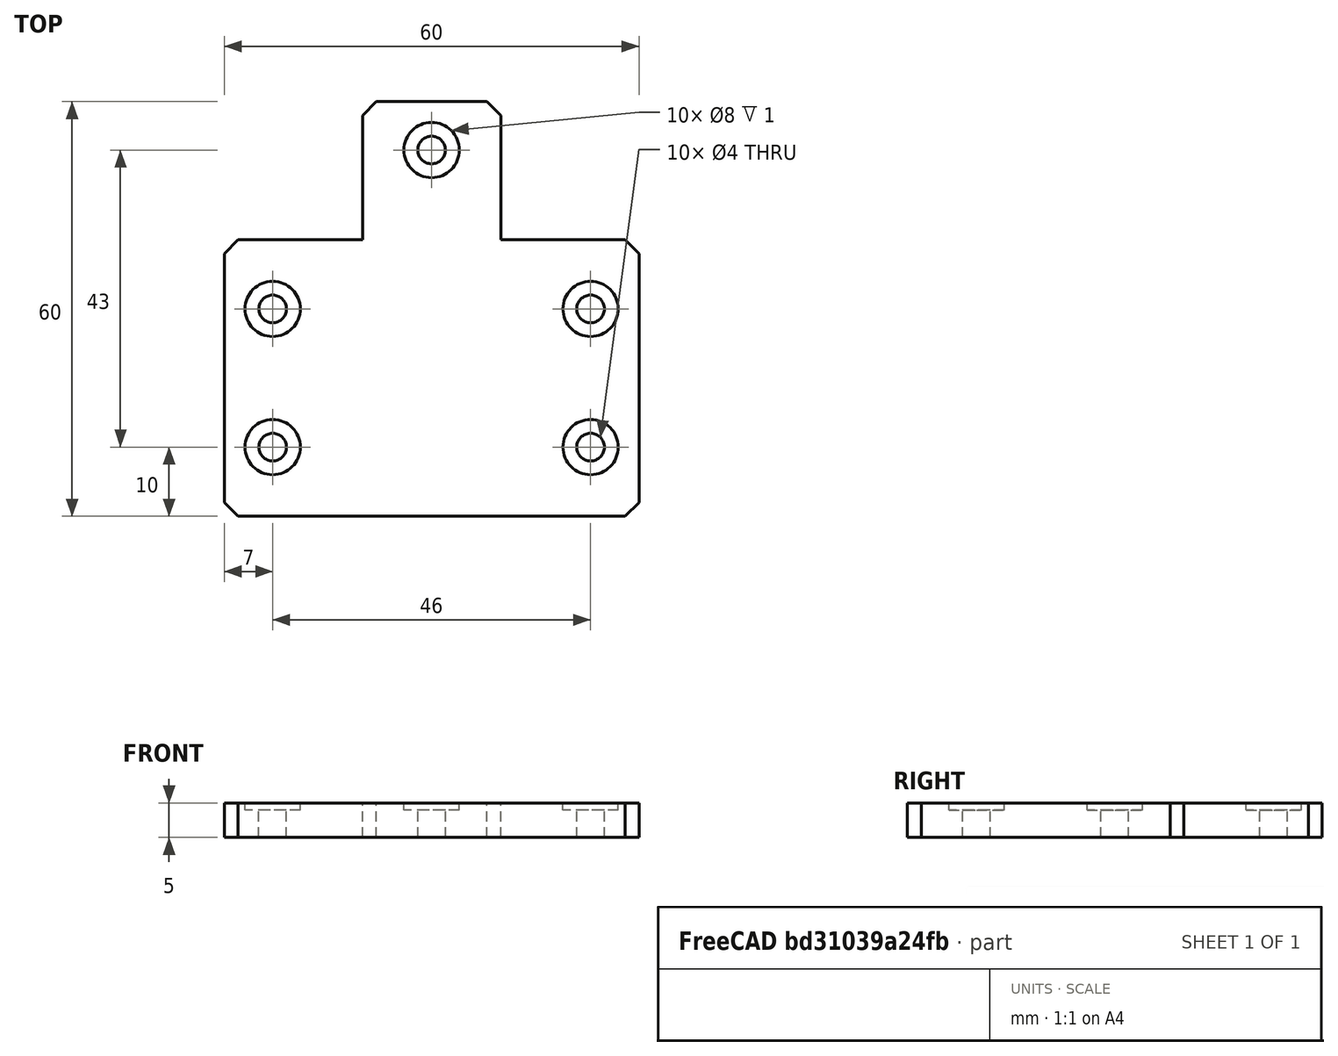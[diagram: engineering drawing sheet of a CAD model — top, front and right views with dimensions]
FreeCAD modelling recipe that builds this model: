
FCSTD DOCUMENT  (FreeCAD 0.18R14555 (Git shallow))
Label: t-bracket
License: All rights reserved
LicenseURL: http://en.wikipedia.org/wiki/All_rights_reserved
objects: Part::Cylinder×10, Part::MultiFuse×3, Part::Box×2, Part::Cut×2, Part::Feature×2, Part::Chamfer×1
note: 20 computed .brp shape members not serialized (recipe doc carries the construction recipe); baked Part::Feature solids carry a one-line shape summary decoded from their .brp

FEATURE [Part::Box] Box  label="Cube"
  AttacherType = Attacher::AttachEngine3D
  Height = 5
  Length = 60
  Width = 40
FEATURE [Part::Box] Box001  label="Cube001"
  AttacherType = Attacher::AttachEngine3D
  Height = 5
  Length = 20
  Placement = pos=(20,40,0) rot=(0,0,1;0rad)
  Width = 20
FEATURE [Part::MultiFuse] Fusion
  Shapes = -> [Box001,Box]
FEATURE [Part::Cylinder] Cylinder
  Angle = 360
  AttacherType = Attacher::AttachEngine3D
  Height = 10
  Placement = pos=(7,10,0) rot=(0,0,1;0rad)
  Radius = 2
FEATURE [Part::Cylinder] Cylinder001
  Angle = 360
  AttacherType = Attacher::AttachEngine3D
  Height = 10
  Placement = pos=(7,30,0) rot=(0,0,1;0rad)
  Radius = 2
FEATURE [Part::Cylinder] Cylinder002
  Angle = 360
  AttacherType = Attacher::AttachEngine3D
  Height = 10
  Placement = pos=(53,10,0) rot=(0,0,1;0rad)
  Radius = 2
FEATURE [Part::Cylinder] Cylinder003
  Angle = 360
  AttacherType = Attacher::AttachEngine3D
  Height = 10
  Placement = pos=(53,30,0) rot=(0,0,1;0rad)
  Radius = 2
FEATURE [Part::Cylinder] Cylinder004
  Angle = 360
  AttacherType = Attacher::AttachEngine3D
  Height = 10
  Placement = pos=(30,53,0) rot=(0,0,1;0rad)
  Radius = 2
FEATURE [Part::Cylinder] Cylinder005
  Angle = 360
  AttacherType = Attacher::AttachEngine3D
  Height = 1
  Placement = pos=(7,30,0) rot=(0,0,1;0rad)
  Radius = 4
FEATURE [Part::Cylinder] Cylinder006
  Angle = 360
  AttacherType = Attacher::AttachEngine3D
  Height = 1
  Placement = pos=(7,10,0) rot=(0,0,1;0rad)
  Radius = 4
FEATURE [Part::Cylinder] Cylinder007
  Angle = 360
  AttacherType = Attacher::AttachEngine3D
  Height = 1
  Placement = pos=(53,10,0) rot=(0,0,1;0rad)
  Radius = 4
FEATURE [Part::Cylinder] Cylinder008
  Angle = 360
  AttacherType = Attacher::AttachEngine3D
  Height = 1
  Placement = pos=(53,30,0) rot=(0,0,1;0rad)
  Radius = 4
FEATURE [Part::Cylinder] Cylinder009
  Angle = 360
  AttacherType = Attacher::AttachEngine3D
  Height = 1
  Placement = pos=(30,53,0) rot=(0,0,1;0rad)
  Radius = 4
FEATURE [Part::MultiFuse] Fusion001
  Placement = pos=(0,0,4) rot=(0,0,1;0rad)
  Shapes = -> [Cylinder006,Cylinder005,Cylinder009,Cylinder008,Cylinder007]
FEATURE [Part::MultiFuse] Fusion002
  Shapes = -> [Cylinder,Cylinder001,Cylinder003,Cylinder004,Cylinder002]
FEATURE [Part::Cut] Cut
  Base = -> Fusion
  Tool = -> Fusion001
FEATURE [Part::Cut] Cut001
  Base = -> Cut
  Tool = -> Fusion002
FEATURE [Part::Chamfer] Chamfer
  Base = -> Cut001
  Edges = 6 edges r=2: [Edge1,Edge3,Edge6,Edge25,Edge39,Edge52]
FEATURE [Part::Feature] Chamfer001
  shape: bbox 60 x 60 x 5 mm, 31 faces (baked)
FEATURE [Part::Feature] Chamfer001_solid  label="Chamfer001 (Solid)"
  shape: bbox 60 x 60 x 5 mm, 31 faces (baked)
